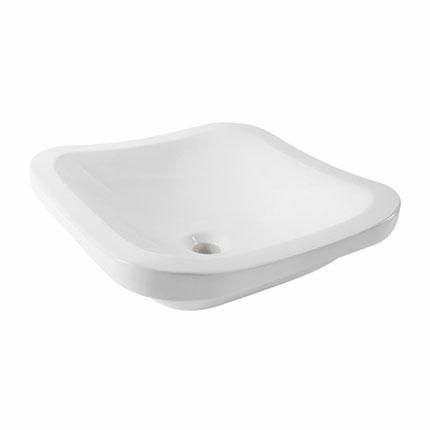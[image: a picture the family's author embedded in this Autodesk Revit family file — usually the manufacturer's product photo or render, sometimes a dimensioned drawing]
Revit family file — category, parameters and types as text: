
# Revit family: LV STALA
name_source: partatom
category: Aparatos sanitarios
revit_build: Autodesk Revit 2016 (Build: 20150220_1215(x64)
units: mm (PartAtom-declared; Revit-internal decimal feet)

## family parameters
Compartido = No
Corte con vacíos al cargar = No
Cota de conector redondo = Diámetro de uso
Número OmniClass = 23.45.00.00
Punto de cálculo de habitación = No
Se basa en plano de trabajo = No
Siempre vertical = Sí
Tipo de pieza = Normal
Título OmniClass = Sanitary, Laundry, and Cleaning Equipment

## types (2) — shared parameters
Comentarios de tipo = SANIVEX
Data Sheet = https://www.helvex.com.mx
Fabricante = HELVEX
Features = Perfect Assembly; Uniformity
High Gloss Ceramic = High Gloss Ceramic
Instructive = https://www.helvex.com.mx
Total Length = 18"
URL = https://www.helvex.com.mx

## per-type parameters (varying)
| type | Descripción | Imagen de tipo | Total Height | Total Width |
| LV LUCERNA3 | LAVABO LUCERNA TRES PERFORACIONES DE SOBREPONER CON REBOSADERO | <Ninguno> | 5" | 22" |
| LV STALA | Lavabo de sobreponer y sobrecubierta sin rebosadero | LV STALA.jpg | 6" | 18" |

note: column(s) folded — value = type name in every type: Modelo

## geometry (parser evidence)
native form markers: Sweep x3
no freeform markers — native parametric forms only
